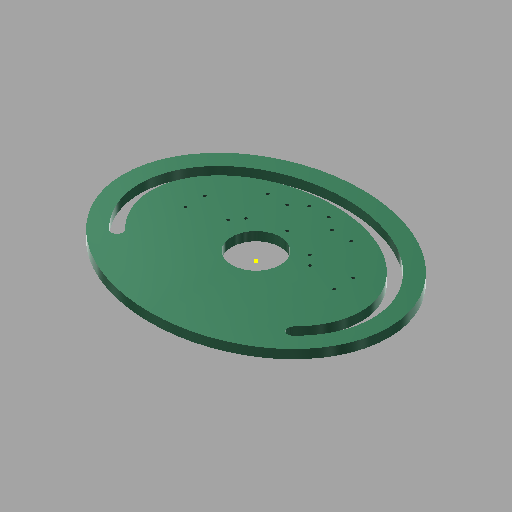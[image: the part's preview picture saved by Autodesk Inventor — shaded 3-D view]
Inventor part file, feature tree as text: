
AUTODESK INVENTOR PART (.ipt)
format: ipt  version: 2024.3 (Build 283343000, 343)  size: 325,120 bytes
history: native  units: mm
features: reference x16, sketch x4, extrude x3, other x3, hole x1, projected_geometry x1
ambient origin geometry x8: Origin, YZ Plane, XZ Plane, XY Plane, X Axis, Y Axis, Z Axis, Center Point
bodies: Volumenkörper1 (feature_tree)
feature tree (28):
  extrude  "Extrusion1"  Depth=240.0mm
  extrude  "Extrusion2"  Depth=10.0mm
  extrude  "Extrusion4"  Depth=31.5mm
  hole  "Bohrung1"  [1 undecoded]
  sketch  "Skizze6"  dims[d10=31.5mm d11=45.0deg d12=90.0deg d13=12.894099mm d14=30.0deg d15=30.0deg d16=0.0mm d17=0.0mm d20=0.0mm d21=0.0mm d22=3.242mm d23=8.0mm d24=4.0mm d25=2.0mm d26=90.0deg d27=8.0mm d28=20.594885mm]
  sketch  "Skizze2"  dims[d0=300.0mm d1=240.0mm]
  projected_geometry  "Projizierte Kontur1"
  sketch  "Skizze4"  dims[d2=10.0mm d3=0.0mm d7=18.5mm]
  reference  "Referenz2"
  sketch  "Skizze5"  dims[d8=18.5mm d9=31.5mm]
  reference  "Referenz3"
  reference  "Referenz4"
  reference  "Referenz5"
  reference  "Referenz6"
  reference  "Referenz7"
  reference  "Referenz8"
  reference  "Referenz9"
  reference  "Referenz10"
  reference  "Referenz11"
  reference  "Referenz12"
  reference  "Referenz13"
  reference  "Referenz14"
  reference  "Referenz15"
  reference  "Referenz16"
  reference  "Referenz17"
  other  "<path> - Kompass, Gehäuse\24_0497_0001.iam"
  other  "24_0497_0001.iam"
  other  "Alle_Schalter:1"
note: 1 required parameter value undecoded (feature->parameter linkage not recoverable at this tier; creation-order binding heuristic only, values carry confidence <= 0.55)
note: 1 file-system path scrubbed to <path> (originals preserved in map.json)
